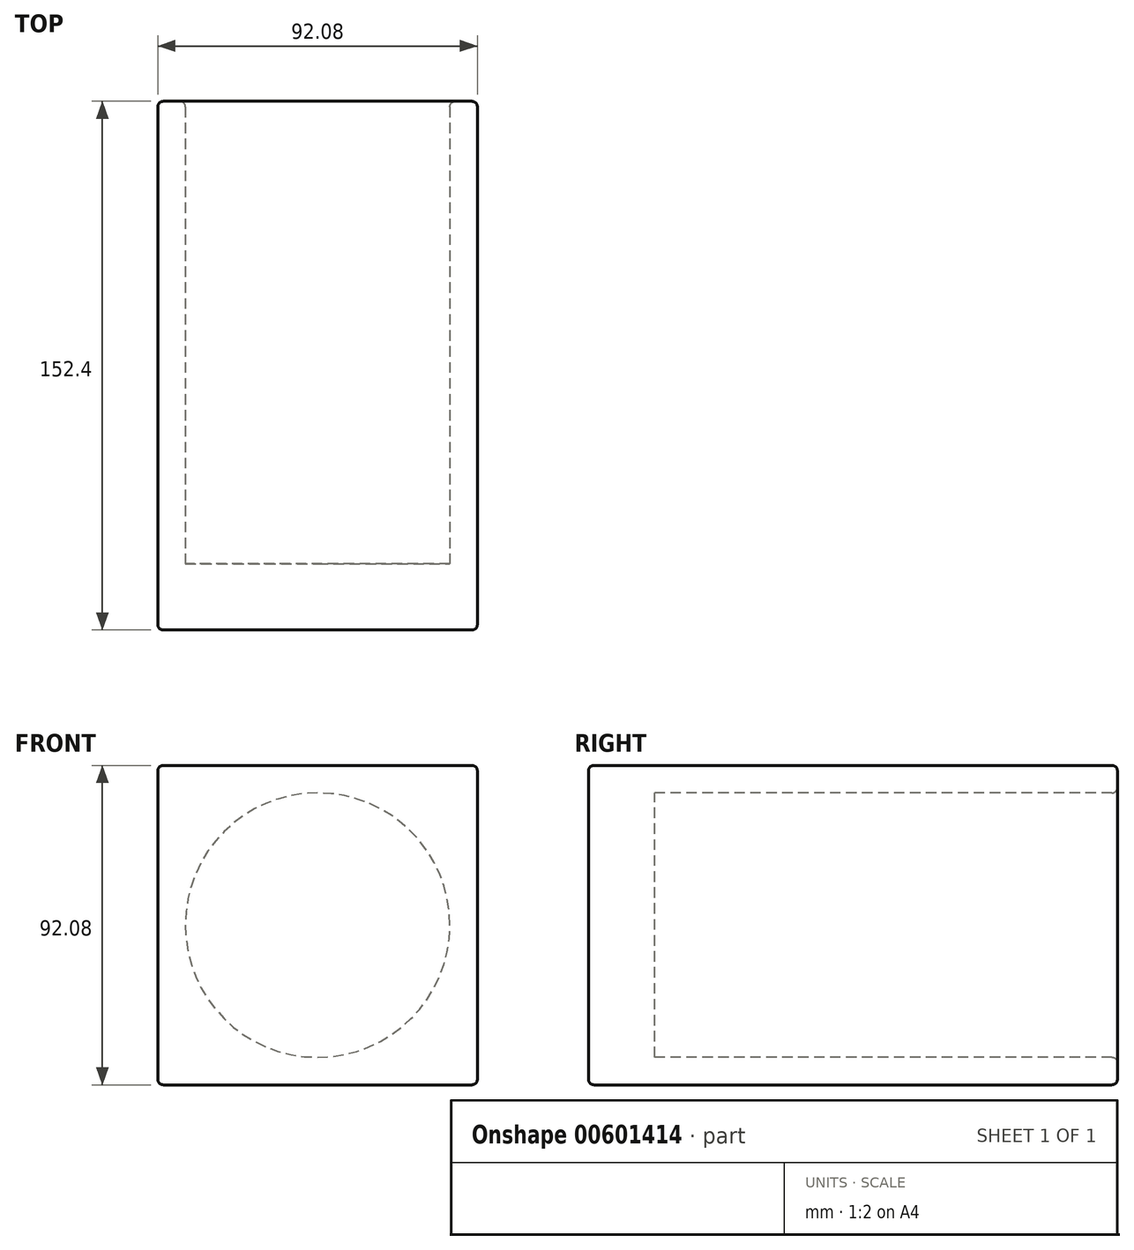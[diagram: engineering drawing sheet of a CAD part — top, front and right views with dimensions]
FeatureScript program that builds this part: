
annotation { "Feature Type Name" : "Feature", "Feature Type Description" : "" }
export const myFeature = defineFeature(function(context is Context, id is Id, definition is map)
    precondition{}
    {
        {
            var Q0;
            Q0=qCreatedBy(makeId("Front.planeOp"),FACE);
            var sketch = newSketch(context, id + "F0", { "sketchPlane" : qUnion([Q0])});
            skLineSegment(sketch, "E0.bottom", {"start": v(-46.04, 46.04) * mm, "end": v(46.04, 46.04) * mm});
            skLineSegment(sketch, "E0.top", {"start": v(-46.04, -46.04) * mm, "end": v(46.04, -46.04) * mm});
            skLineSegment(sketch, "E0.left", {"start": v(-46.04, 46.04) * mm, "end": v(-46.04, -46.04) * mm});
            skLineSegment(sketch, "E0.right", {"start": v(46.04, 46.04) * mm, "end": v(46.04, -46.04) * mm});
            skPoint(sketch, "E0.middle", {"position": v(0, 0) * mm});
            skCircle(sketch, "E1", {"center": v(0, 0) * mm, "radius": 38.1 * mm});
            skSolve(sketch);
        }
        {
            var Q0;
            Q0=makeQuery(id+"F0.imprint","IMPRINT",FACE,{"disambiguationData":[TD([[makeQuery(id+"F0.imprint","IMPRINT",EDGE,{"derivedFrom":sQuery(id+"F0.wireOp",EDGE,"E0.bottom")}),-1.0]])]});
            extrude(context, id + "F1", {"entities" : qUnion([Q0]), "oppositeDirection" : true, "depth" : 152.4 * mm, "offsetDistance" : 25.4 * mm});
        }
        {
            var Q0;
            Q0=makeQuery(id+"F0.imprint","IMPRINT",FACE,{"disambiguationData":[TD([[makeQuery(id+"F0.imprint","IMPRINT",EDGE,{"derivedFrom":sQuery(id+"F0.wireOp",EDGE,"E1")}),1.0]])]});
            var Q1;
            Q1=makeQuery(id+"F0.imprint","IMPRINT",FACE,{"disambiguationData":[TD([[makeQuery(id+"F0.imprint","IMPRINT",EDGE,{"derivedFrom":sQuery(id+"F0.wireOp",EDGE,"E0.bottom")}),-1.0]])]});
            extrude(context, id + "F2", {"entities" : qUnion([Q0, Q1]), "operationType" : NewBodyOperationType.ADD, "oppositeDirection" : true, "depth" : 19.05 * mm, "offsetDistance" : 25.4 * mm});
        }
        {
            var Q0;
            Q0=makeQuery(id+"F1.opExtrude","SWEPT_EDGE",EDGE,{"disambiguationData":[OSD([sQuery(id+"F0.wireOp",EDGE,"E0.bottom"),sQuery(id+"F0.wireOp",EDGE,"E0.left")])]});
            var Q1;
            Q1=makeQuery(id+"F1.opExtrude","SWEPT_EDGE",EDGE,{"disambiguationData":[OSD([sQuery(id+"F0.wireOp",EDGE,"E0.top"),sQuery(id+"F0.wireOp",EDGE,"E0.left")])]});
            var Q2;
            Q2=makeQuery(id+"F1.opExtrude","SWEPT_EDGE",EDGE,{"disambiguationData":[OSD([sQuery(id+"F0.wireOp",EDGE,"E0.bottom"),sQuery(id+"F0.wireOp",EDGE,"E0.right")])]});
            var Q3;
            Q3=makeQuery(id+"F1.opExtrude","SWEPT_FACE",FACE,{"disambiguationData":[OSD([sQuery(id+"F0.wireOp",EDGE,"E0.right")])]});
            var Q4;
            {var subQ0=sQuery(id+"F0.wireOp",EDGE,"E0.right");var subQ1=sQuery(id+"F0.wireOp",EDGE,"E0.left");var subQ2=sQuery(id+"F0.wireOp",EDGE,"E0.top");var subQ3=sQuery(id+"F0.wireOp",EDGE,"E0.bottom");Q4=makeQuery(id+"F2.boolean.opBoolean","MERGE",FACE,{"derivedFrom":[makeQuery(id+"F1.opExtrude","CAP_FACE",FACE,{"disambiguationData":[OSD([subQ3,subQ2,subQ1,subQ0,sQuery(id+"F0.wireOp",EDGE,"E1")])],"isStart":true}),makeQuery(id+"F2.opExtrude","CAP_FACE",FACE,{"disambiguationData":[OSD([subQ3,subQ2,subQ1,subQ0])],"isStart":true})]});}
            var Q5;
            Q5=makeQuery(id+"F1.opExtrude","CAP_EDGE",EDGE,{"disambiguationData":[OSD([sQuery(id+"F0.wireOp",EDGE,"E0.top")])],"isStart":false});
            var Q6;
            Q6=makeQuery(id+"F1.opExtrude","CAP_EDGE",EDGE,{"disambiguationData":[OSD([sQuery(id+"F0.wireOp",EDGE,"E0.left")])],"isStart":false});
            var Q7;
            Q7=makeQuery(id+"F1.opExtrude","CAP_EDGE",EDGE,{"disambiguationData":[OSD([sQuery(id+"F0.wireOp",EDGE,"E0.bottom")])],"isStart":false});
            var Q8;
            Q8=makeQuery(id+"F1.opExtrude","CAP_EDGE",EDGE,{"disambiguationData":[OSD([sQuery(id+"F0.wireOp",EDGE,"E1")])],"isStart":false});
            fillet(context, id + "F3", {"entities" : qUnion([Q0, Q1, Q2, Q3, Q4, Q5, Q6, Q7, Q8]), "radius" : 1.59 * mm, "tangentPropagation" : true, "allowEdgeOverflow" : false});
        }
    });
